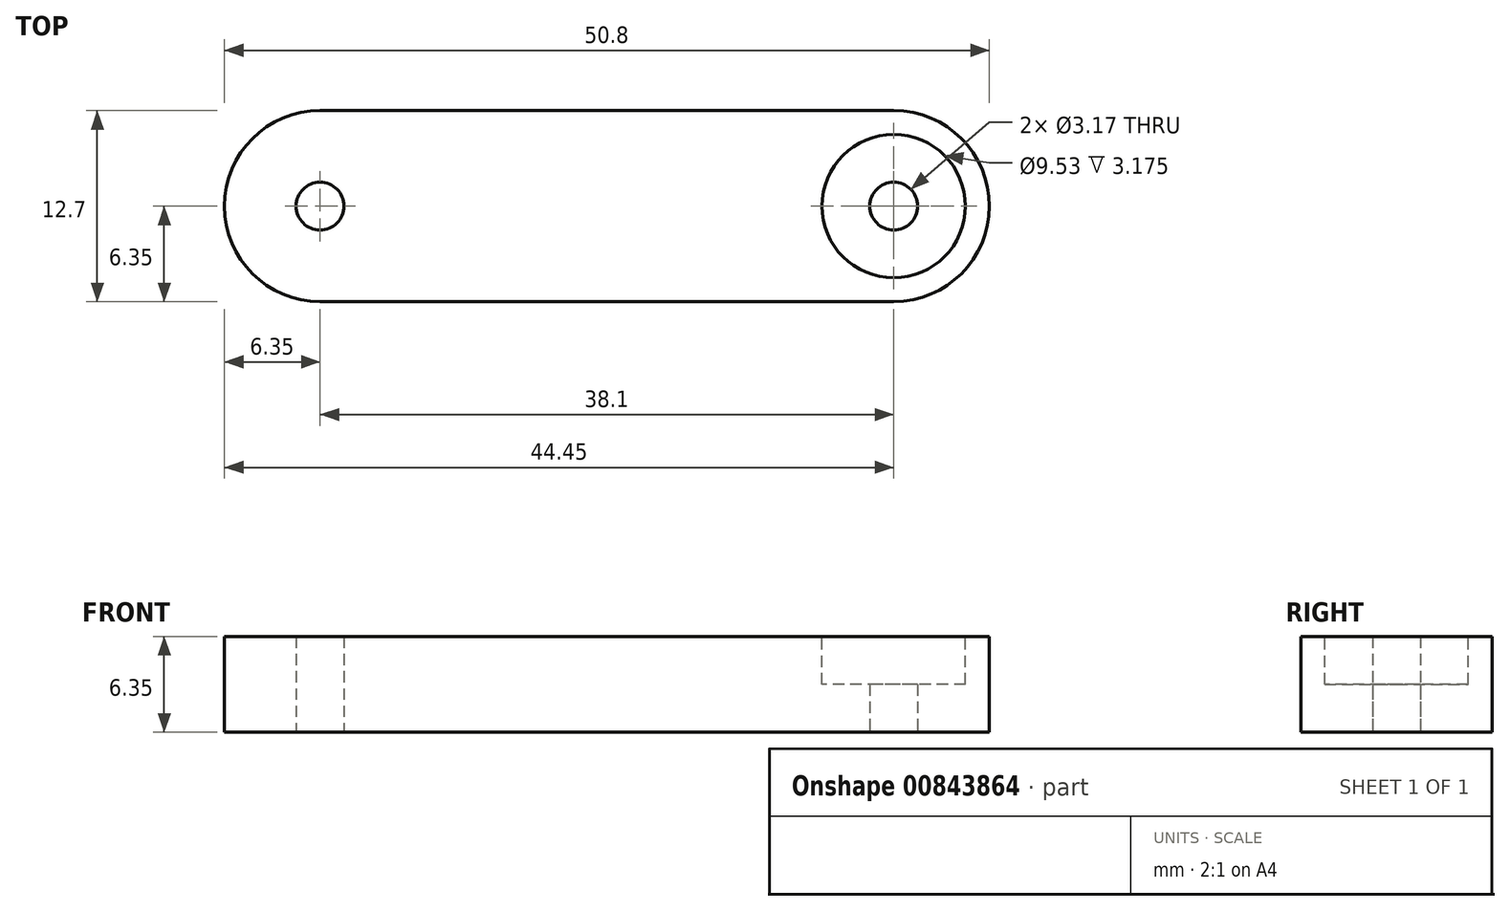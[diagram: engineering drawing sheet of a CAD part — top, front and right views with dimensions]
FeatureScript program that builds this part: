
annotation { "Feature Type Name" : "Feature", "Feature Type Description" : "" }
export const myFeature = defineFeature(function(context is Context, id is Id, definition is map)
    precondition{}
    {
        {
            var Q0;
            Q0=qCreatedBy(makeId("Top.planeOp"),FACE);
            var sketch = newSketch(context, id + "F0", { "sketchPlane" : qUnion([Q0])});
            skCircle(sketch, "E0", {"center": v(0, 0) * mm, "radius": 6.35 * mm});
            skCircle(sketch, "E1", {"center": v(38.1, 0) * mm, "radius": 6.35 * mm});
            skLineSegment(sketch, "E2", {"start": v(0, 6.35) * mm, "end": v(38.1, 6.35) * mm});
            skLineSegment(sketch, "E3", {"start": v(0, -6.35) * mm, "end": v(38.1, -6.35) * mm});
            skCircle(sketch, "E4", {"center": v(0, 0) * mm, "radius": 1.59 * mm});
            skCircle(sketch, "E5", {"center": v(38.1, 0) * mm, "radius": 1.59 * mm});
            skSolve(sketch);
        }
        {
            var Q0;
            {var subQ0=sQuery(id+"F0.wireOp",EDGE,"E2");Q0=makeQuery(id+"F0.imprint","IMPRINT",FACE,{"disambiguationData":[TD([[makeQuery(id+"F0.imprint","IMPRINT",EDGE,{"derivedFrom":subQ0}),-1.0]])]});}
            var Q1;
            Q1=makeQuery(id+"F0.imprint","IMPRINT",FACE,{"disambiguationData":[TD([[makeQuery(id+"F0.imprint","IMPRINT",EDGE,{"derivedFrom":sQuery(id+"F0.wireOp",EDGE,"E5")}),-1.0]])]});
            var Q2;
            Q2=makeQuery(id+"F0.imprint","IMPRINT",FACE,{"disambiguationData":[TD([[makeQuery(id+"F0.imprint","IMPRINT",EDGE,{"derivedFrom":sQuery(id+"F0.wireOp",EDGE,"E4")}),-1.0]])]});
            extrude(context, id + "F1", {"entities" : qUnion([Q0, Q1, Q2]), "depth" : 6.35 * mm, "offsetDistance" : 25.4 * mm});
        }
        {
            var Q0;
            Q0=makeQuery(id+"F1.opExtrude","CAP_FACE",FACE,{"disambiguationData":[OSD([sQuery(id+"F0.wireOp",EDGE,"E0"),sQuery(id+"F0.wireOp",EDGE,"E1"),sQuery(id+"F0.wireOp",EDGE,"E2"),sQuery(id+"F0.wireOp",EDGE,"E3"),sQuery(id+"F0.wireOp",EDGE,"E4"),sQuery(id+"F0.wireOp",EDGE,"E5")])],"isStart":false});
            var sketch = newSketch(context, id + "F2", { "sketchPlane" : qUnion([Q0])});
            skCircle(sketch, "E6.0", {"center": v(38.1, 0) * mm, "radius": 4.76 * mm});
            skSolve(sketch);
        }
        {
            var Q0;
            Q0 = qSketchRegion(id + "F2", true);
            extrude(context, id + "F3", {"entities" : qUnion([Q0]), "operationType" : NewBodyOperationType.REMOVE, "oppositeDirection" : true, "depth" : 3.17 * mm, "offsetDistance" : 25.4 * mm});
        }
    });
